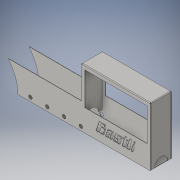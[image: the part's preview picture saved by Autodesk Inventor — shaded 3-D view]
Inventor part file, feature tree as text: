
AUTODESK INVENTOR PART (.ipt)
format: ipt  version: 2016 (Build 200138000, 138)  size: 681,472 bytes
history: native  units: in
note: dims shown in document units (in); Inventor stores cm internally (conversion verified against a paired STEP export)
features: sketch x15, other x11, sheet_metal_op x11, projected_geometry x4, mirror x3, chamfer x2, extrude x2, plane x1
ambient origin geometry x8: Origin, YZ Plane, XZ Plane, XY Plane, X Axis, Y Axis, Z Axis, Center Point
bodies: Solid1 (feature_tree)
feature tree (49):
  other  "Blade.ipt"
  sheet_metal_op  "Face1"
  plane  "Work Plane1"
  mirror  "Mirror1"
  sheet_metal_op  "Bend1"
  mirror  "Mirror2"
  other  "A-Side Definition"
  sheet_metal_op  "Flange1"
  sheet_metal_op  "Flange2"
  mirror  "Mirror3"
  sheet_metal_op  "Flange3"
  chamfer  "Corner Round1"
  chamfer  "Corner Round2"
  extrude  "Extrusion1"  Depth=0.0394in
  extrude  "Extrusion2"  Depth=0.0394in
  sketch  "Sketch1"  dims[d0=0.3937in d1=0.0394in]
  sketch  "Sketch6"  dims[d2=-1.25in d3=0.0394in]
  sketch  "Sketch10"  dims[d7=0.0394in]
  sketch  "Sketch12"  dims[d21=0.0in]
  sketch  "Sketch13"  dims[d23=0.0394in]
  sketch  "Sketch7"  dims[d4=0.0197in]
  other  "Plate1"
  sketch  "Sketch8"  dims[d5=0.0787in]
  sketch  "Sketch9"  dims[d6=0.0394in]
  other  "Plate2"
  sheet_metal_op  "Bend4"
  sheet_metal_op  "Corner1"
  sketch  "Sketch11"  dims[d20=0.0394in]
  other  "Plate3"
  sheet_metal_op  "Bend5"
  sheet_metal_op  "Corner2"
  sketch  "Sketch14"  dims[d24=0.0197in]
  projected_geometry  "Projected Loop1"
  sketch  "Sketch15"  dims[d25=0.0787in]
  projected_geometry  "Projected Loop2"
  sketch  "Sketch16"  dims[d26=0.0394in]
  other  "Plate4"
  sheet_metal_op  "Bend6"
  sheet_metal_op  "Corner3"
  sketch  "Sketch17"  dims[d27=6.0in d28=90.0deg d29=0.0394in]
  sketch  "Sketch18"  dims[d30=0.1575in]
  sketch  "Sketch19"  dims[d31=0.0394in d32=0.0394in d33=0.0394in d34=0.0197in d35=0.0787in d36=0.0394in d37=6.0in d38=90.0deg d39=0.0394in d40=0.0in d41=0.1575in d42=0.0394in d43=0.0394in d44=0.0394in d45=0.0in d46=0.3937in d47=0.3937in d48=0.3937in d51=1.5748in d52=0.0394in d53=0.0in d54=0.5in d55=0.0394in d56=0.0197in d57=0.0787in d58=0.0394in d59=6.0in d60=90.0deg d61=0.0394in d62=0.0in d63=0.1575in d64=0.0394in d65=0.0394in d66=0.0787in d67=0.0787in d68=6.0in d69=1.5748in d70=0.0787in d71=0.0in d72=1.0in d73=0.0in d74=1.0in d75=0.0in]
  projected_geometry  "Projected Loop3"
  projected_geometry  "Projected Loop4"
  other  "Cut1"
  other  "Cut2"
  other  "Cut3"
  other  "Cut4"
  other  "Definition1"
